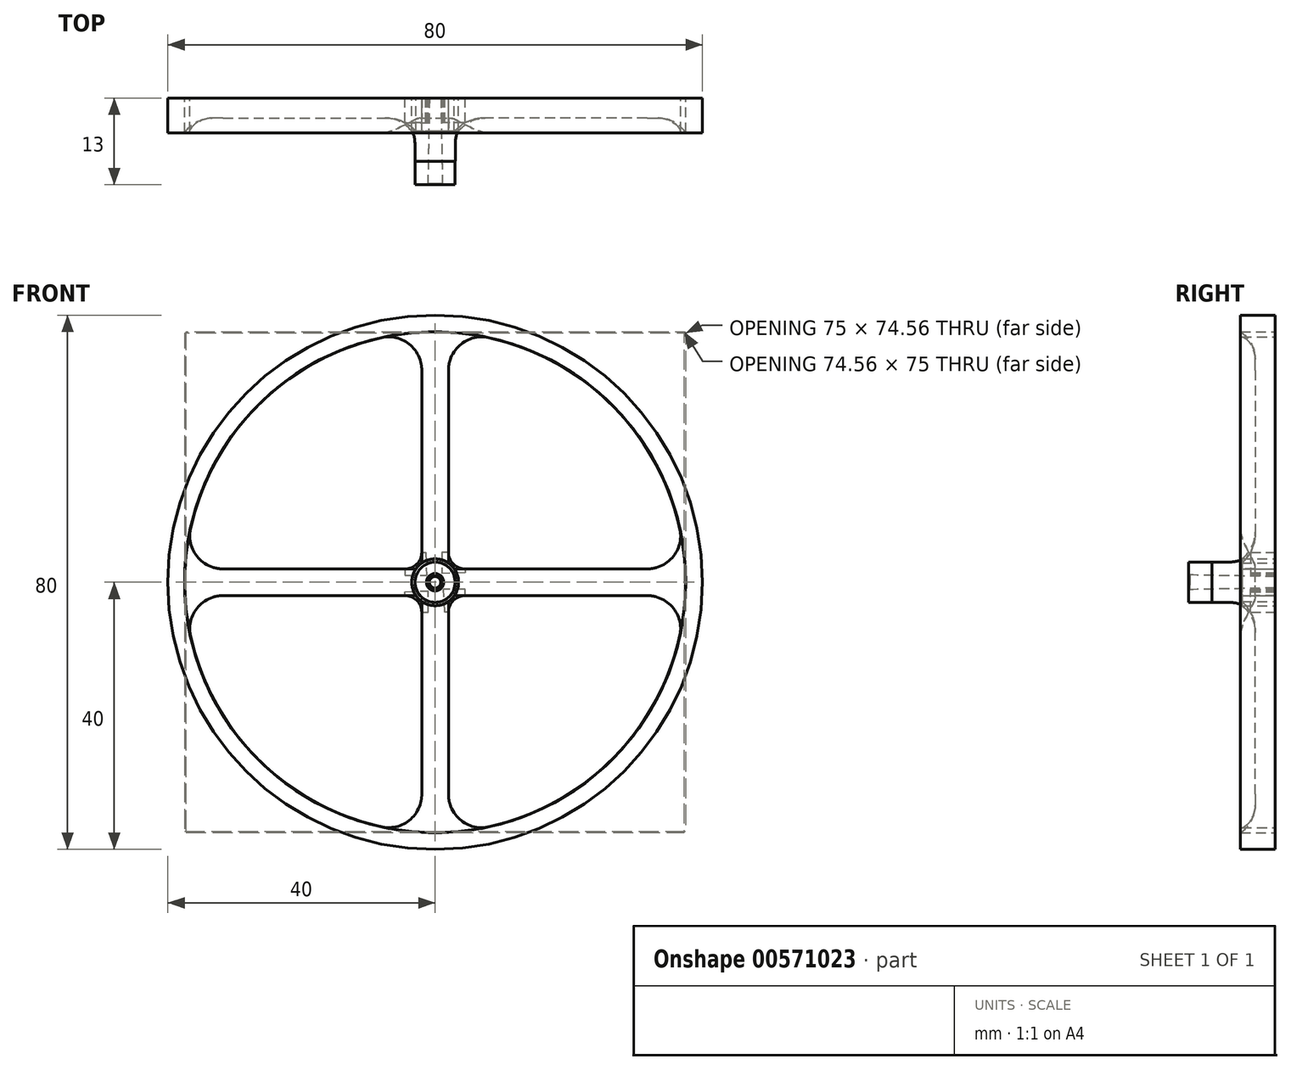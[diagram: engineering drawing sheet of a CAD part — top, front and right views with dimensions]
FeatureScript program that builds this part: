
annotation { "Feature Type Name" : "Feature", "Feature Type Description" : "" }
export const myFeature = defineFeature(function(context is Context, id is Id, definition is map)
    precondition{}
    {
        {
            var Q0;
            Q0=qCreatedBy(makeId("Front.planeOp"),FACE);
            var sketch = newSketch(context, id + "F0", { "sketchPlane" : qUnion([Q0])});
            skCircle(sketch, "E0", {"center": v(0, 0) * mm, "radius": 3.5 * mm});
            skSolve(sketch);
        }
        {
            var Q0;
            Q0=qSketchRegion(id+"F0",true);
            extrude(context, id + "F1", {"entities" : qUnion([Q0]), "depth" : 5 * mm});
        }
        {
            var Q0;
            Q0=qCreatedBy(makeId("Right.planeOp"),FACE);
            var sketch = newSketch(context, id + "F2", { "sketchPlane" : qUnion([Q0])});
            skLineSegment(sketch, "E1", {"start": v(3.77, 0) * mm, "end": v(-36.31, 0) * mm, "construction": true});
            skLineSegment(sketch, "E2", {"start": v(-13, 0) * mm, "end": v(-13, 3) * mm});
            skLineSegment(sketch, "E3", {"start": v(-13, 3) * mm, "end": v(-9.5, 3) * mm});
            skFitSpline(sketch, "E4", {"points": [v(-9.5, 3) * mm, v(-5, 3.5) * mm], "startDerivative": vector(5.34, 0.31) * mm, "endDerivative": vector(2.38, 2.14) * mm});
            skLineSegment(sketch, "E5", {"start": v(-5, 3.5) * mm, "end": v(-5, 0) * mm});
            skLineSegment(sketch, "E6", {"start": v(-5, 0) * mm, "end": v(-13, 0) * mm});
            skSolve(sketch);
        }
        {
            var Q0;
            Q0=qSketchRegion(id+"F2",true);
            var Q1;
            Q1=sQuery(id+"F2.wireOp",EDGE,"E1");
            revolve(context, id + "F3", {"operationType" : NewBodyOperationType.ADD, "entities" : qUnion([Q0]), "axis" : qUnion([Q1]), "revolveType" : RevolveType.FULL});
        }
        {
            var Q0;
            Q0=makeQuery(id+"F1.opExtrude","CAP_FACE",FACE,{"disambiguationData":[OSD([sQuery(id+"F0.wireOp",EDGE,"E0")])],"isStart":true});
            var sketch = newSketch(context, id + "F4", { "sketchPlane" : qUnion([Q0])});
            skCircle(sketch, "E7", {"center": v(0, 0) * mm, "radius": 0.85 * mm});
            skSolve(sketch);
        }
        {
            var Q0;
            Q0=qSketchRegion(id+"F4",true);
            extrude(context, id + "F5", {"entities" : qUnion([Q0]), "operationType" : NewBodyOperationType.REMOVE, "endBound" : BoundingType.THROUGH_ALL, "oppositeDirection" : true, "depth" : 25 * mm, "hasDraft" : true, "draftAngle" : 1.1 * degree, "offsetDistance" : 25 * mm});
        }
        {
            var Q0;
            Q0=qCreatedBy(makeId("Top.planeOp"),FACE);
            var sketch = newSketch(context, id + "F6", { "sketchPlane" : qUnion([Q0])});
            skLineSegment(sketch, "E8.bottom", {"start": v(-2, 0) * mm, "end": v(2, 0) * mm});
            skLineSegment(sketch, "E8.top", {"start": v(-2, -3) * mm, "end": v(2, -3) * mm});
            skLineSegment(sketch, "E8.left", {"start": v(-2, 0) * mm, "end": v(-2, -3) * mm});
            skLineSegment(sketch, "E8.right", {"start": v(2, 0) * mm, "end": v(2, -3) * mm});
            skSolve(sketch);
        }
        {
            var Q0;
            Q0=qSketchRegion(id+"F6",true);
            extrude(context, id + "F7", {"entities" : qUnion([Q0]), "operationType" : NewBodyOperationType.ADD, "depth" : 38 * mm, "hasSecondDirection" : true, "secondDirectionOppositeDirection" : false, "secondDirectionDepth" : 2.5 * mm, "offsetDistance" : 25 * mm});
        }
        {
            var Q0;
            Q0=makeQuery(id+"F5.boolean.opBoolean","INTERSECT",EDGE,{"derivedFrom":[makeQuery(id+"F3.opRevolve","SWEPT_FACE",FACE,{"disambiguationData":[OSD([sQuery(id+"F2.wireOp",EDGE,"E2")])]}),makeQuery(id+"F5.opExtrude","SWEPT_FACE",FACE,{"disambiguationData":[OSD([sQuery(id+"F4.wireOp",EDGE,"E7")])]})]});
            chamfer(context, id + "F8", {"entities" : qUnion([Q0]), "width" : .2 * mm, "tangentPropagation" : true});
        }
        {
            var Q0;
            Q0=makeQuery(id+"F7.boolean.opBoolean","MERGE",FACE,{"derivedFrom":[makeQuery(id+"F1.opExtrude","CAP_FACE",FACE,{"disambiguationData":[OSD([sQuery(id+"F0.wireOp",EDGE,"E0")])],"isStart":true}),makeQuery(id+"F7.opExtrude","SWEPT_FACE",FACE,{"disambiguationData":[OSD([sQuery(id+"F6.wireOp",EDGE,"E8.bottom")])]})]});
            var sketch = newSketch(context, id + "F9", { "sketchPlane" : qUnion([Q0])});
            skCircle(sketch, "E9", {"center": v(0, 0) * mm, "radius": 40 * mm});
            skCircle(sketch, "E10", {"center": v(0, 0) * mm, "radius": 37.5 * mm});
            skSolve(sketch);
        }
        {
            var Q0;
            Q0=qSketchRegion(id+"F9",true);
            extrude(context, id + "F10", {"entities" : qUnion([Q0]), "operationType" : NewBodyOperationType.ADD, "oppositeDirection" : true, "depth" : 5.2 * mm});
        }
        {
            var Q0;
            Q0=makeQuery(id+"F7.boolean.opBoolean","INTERSECT",EDGE,{"derivedFrom":[makeQuery(id+"F1.opExtrude","SWEPT_FACE",FACE,{"disambiguationData":[OSD([sQuery(id+"F0.wireOp",EDGE,"E0")])]}),makeQuery(id+"F7.opExtrude","SWEPT_FACE",FACE,{"disambiguationData":[OSD([sQuery(id+"F6.wireOp",EDGE,"E8.top")])]})]});
            var Q1;
            Q1=makeQuery(id+"F10.boolean.opBoolean","INTERSECT",EDGE,{"derivedFrom":[makeQuery(id+"F7.opExtrude","SWEPT_FACE",FACE,{"disambiguationData":[OSD([sQuery(id+"F6.wireOp",EDGE,"E8.top")])]}),makeQuery(id+"F10.opExtrude","SWEPT_FACE",FACE,{"disambiguationData":[OSD([sQuery(id+"F9.wireOp",EDGE,"E10")])]})]});
            fillet(context, id + "F11", {"entities" : qUnion([Q0, Q1]), "radius" : 5 * mm, "tangentPropagation" : true, "allowEdgeOverflow" : false});
        }
        {
            var Q0;
            Q0=makeQuery(id+"F10.boolean.opBoolean","INTERSECT",EDGE,{"derivedFrom":[makeQuery(id+"F7.opExtrude","SWEPT_FACE",FACE,{"disambiguationData":[OSD([sQuery(id+"F6.wireOp",EDGE,"E8.right")])]}),makeQuery(id+"F10.opExtrude","SWEPT_FACE",FACE,{"disambiguationData":[OSD([sQuery(id+"F9.wireOp",EDGE,"E10")])]})]});
            var Q1;
            Q1=makeQuery(id+"F10.boolean.opBoolean","INTERSECT",EDGE,{"derivedFrom":[makeQuery(id+"F7.opExtrude","SWEPT_FACE",FACE,{"disambiguationData":[OSD([sQuery(id+"F6.wireOp",EDGE,"E8.left")])]}),makeQuery(id+"F10.opExtrude","SWEPT_FACE",FACE,{"disambiguationData":[OSD([sQuery(id+"F9.wireOp",EDGE,"E10")])]})]});
            fillet(context, id + "F12", {"entities" : qUnion([Q0, Q1]), "radius" : 5 * mm, "tangentPropagation" : true, "allowEdgeOverflow" : false});
        }
        {
            var Q0;
            Q0=makeQuery(id+"F1.opExtrude","SWEPT_BODY",BODY,{"disambiguationData":[OSD([sQuery(id+"F0.wireOp",EDGE,"E0")])]});
            var Q1;
            Q1=makeQuery(id+"F3.opRevolve","SWEPT_FACE",FACE,{"disambiguationData":[OSD([sQuery(id+"F2.wireOp",EDGE,"E3")])]});
            circularPattern(context, id + "F13", {"entities" : qUnion([Q0]), "axis" : qUnion([Q1]), "angle" : 360 * degree, "instanceCount" : 4, "equalSpace" : true});
        }
        {
            var Q0;
            {var subQ0=makeQuery(id+"F10.boolean.opBoolean","MERGE",FACE,{"derivedFrom":[makeQuery(id+"F7.boolean.opBoolean","MERGE",FACE,{"derivedFrom":[makeQuery(id+"F1.opExtrude","CAP_FACE",FACE,{"disambiguationData":[OSD([sQuery(id+"F0.wireOp",EDGE,"E0")])],"isStart":true}),makeQuery(id+"F7.opExtrude","SWEPT_FACE",FACE,{"disambiguationData":[OSD([sQuery(id+"F6.wireOp",EDGE,"E8.bottom")])]})]}),makeQuery(id+"F10.opExtrude","CAP_FACE",FACE,{"disambiguationData":[OSD([sQuery(id+"F9.wireOp",EDGE,"E9"),sQuery(id+"F9.wireOp",EDGE,"E10")])],"isStart":true})]});Q0=makeQuery(id+"FgIhm2Tt6zTOsJ9_1.boolean.opBoolean","MERGE",FACE,{"derivedFrom":[makeQuery(id+"FDYBKFrb20v7z53_1.opBoolean","MERGE",FACE,{"derivedFrom":[subQ0,makeQuery(id+"F13.opPattern","COPY",FACE,{"derivedFrom":subQ0,"instanceName":"1"}),makeQuery(id+"F13.opPattern","COPY",FACE,{"derivedFrom":subQ0,"instanceName":"2"}),makeQuery(id+"F13.opPattern","COPY",FACE,{"derivedFrom":subQ0,"instanceName":"3"})]}),makeQuery(id+"FgIhm2Tt6zTOsJ9_1.opExtrude","CAP_FACE",FACE,{"disambiguationData":[OSD([sQuery(id+"FTYQuE2zEAQoyuF_1.wireOp",EDGE,"2QqTN2Jg-TwYb-xefx-Ns2m-0Et6M2J3xaq2"),sQuery(id+"FTYQuE2zEAQoyuF_1.wireOp",EDGE,"eRERD4EF-URZr-QwCf-6lY6-XNeSWXYZj7bk"),sQuery(id+"FTYQuE2zEAQoyuF_1.wireOp",EDGE,"w1udHuFG-gaxB-rpRy-TvAe-Q6hEAi3vOdkO"),sQuery(id+"FTYQuE2zEAQoyuF_1.wireOp",EDGE,"ccb8e607-9a5f-4511-8021-514936b70c73.filletArc"),sQuery(id+"FTYQuE2zEAQoyuF_1.wireOp",EDGE,"0a0adc1d-e557-4132-b897-d3ac198357fb.filletArc"),sQuery(id+"FTYQuE2zEAQoyuF_1.wireOp",EDGE,"b0aMqVTr-uXCx-4wKI-6uIc-G6YGe43DG1Aq"),sQuery(id+"FTYQuE2zEAQoyuF_1.wireOp",EDGE,"I1tABSEo-hI8d-lGJT-UJOT-oiTtTxIxys52"),sQuery(id+"FTYQuE2zEAQoyuF_1.wireOp",EDGE,"LAcF6vfi-sfcO-sjto-NgG3-pIlErQrigMXa"),sQuery(id+"FTYQuE2zEAQoyuF_1.wireOp",EDGE,"aqtcTmt6-T24C-q2HQ-cTpA-Y39zHsUlbNQ4")])],"isStart":true})]});}
            var sketch = newSketch(context, id + "F14", { "sketchPlane" : qUnion([Q0])});
            skArc(sketch, "E11", {"start": v(-4.5, 2) * mm, "mid": v(-2.73, 2.73) * mm, "end": v(-2, 4.5) * mm});
            skLineSegment(sketch, "E12", {"start": v(-2, 4.5) * mm, "end": v(-1.03, 4.5) * mm});
            skLineSegment(sketch, "E13", {"start": v(-1.03, 4.5) * mm, "end": v(-1.03, 1.28) * mm});
            skLineSegment(sketch, "E14", {"start": v(-4.5, 2) * mm, "end": v(-4.5, 1.43) * mm});
            skLineSegment(sketch, "E15", {"start": v(-4.5, 1.43) * mm, "end": v(-1.03, 1.28) * mm});
            skLineSegment(sketch, "E16.1.0", {"start": v(-4.5, -2) * mm, "end": v(-4.5, -1.03) * mm});
            skLineSegment(sketch, "E16.1.1", {"start": v(-4.5, -1.03) * mm, "end": v(-1.28, -1.03) * mm});
            skLineSegment(sketch, "E16.1.2", {"start": v(-1.43, -4.5) * mm, "end": v(-1.28, -1.03) * mm});
            skLineSegment(sketch, "E16.1.3", {"start": v(-2, -4.5) * mm, "end": v(-1.43, -4.5) * mm});
            skArc(sketch, "E16.1.4", {"start": v(-2, -4.5) * mm, "mid": v(-2.73, -2.73) * mm, "end": v(-4.5, -2) * mm});
            skLineSegment(sketch, "E16.2.0", {"start": v(2, -4.5) * mm, "end": v(1.03, -4.5) * mm});
            skLineSegment(sketch, "E16.2.1", {"start": v(1.03, -4.5) * mm, "end": v(1.03, -1.28) * mm});
            skLineSegment(sketch, "E16.2.2", {"start": v(4.5, -1.43) * mm, "end": v(1.03, -1.28) * mm});
            skLineSegment(sketch, "E16.2.3", {"start": v(4.5, -2) * mm, "end": v(4.5, -1.43) * mm});
            skArc(sketch, "E16.2.4", {"start": v(4.5, -2) * mm, "mid": v(2.73, -2.73) * mm, "end": v(2, -4.5) * mm});
            skLineSegment(sketch, "E16.3.0", {"start": v(4.5, 2) * mm, "end": v(4.5, 1.03) * mm});
            skLineSegment(sketch, "E16.3.1", {"start": v(4.5, 1.03) * mm, "end": v(1.28, 1.03) * mm});
            skLineSegment(sketch, "E16.3.2", {"start": v(1.43, 4.5) * mm, "end": v(1.28, 1.03) * mm});
            skLineSegment(sketch, "E16.3.3", {"start": v(2, 4.5) * mm, "end": v(1.43, 4.5) * mm});
            skArc(sketch, "E16.3.4", {"start": v(2, 4.5) * mm, "mid": v(2.73, 2.73) * mm, "end": v(4.5, 2) * mm});
            skPoint(sketch, "E16.center", {"position": v(0, 0) * mm});
            skSolve(sketch);
        }
        {
            var Q0;
            Q0=qSketchRegion(id+"F14",true);
            extrude(context, id + "F15", {"entities" : qUnion([Q0]), "oppositeDirection" : true, "depth" : 3.7 * mm});
        }
    });
